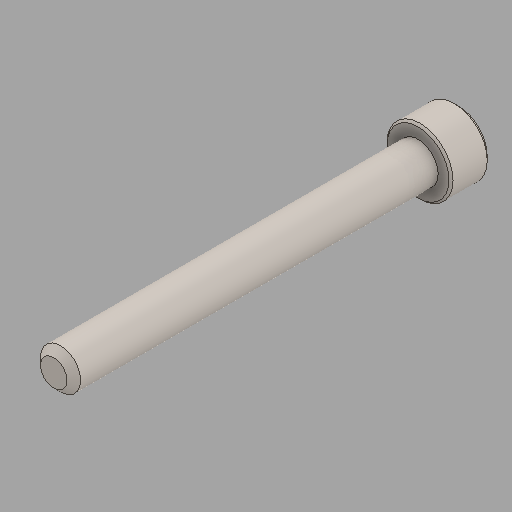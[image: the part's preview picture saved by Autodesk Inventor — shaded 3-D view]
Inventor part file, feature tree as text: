
AUTODESK INVENTOR PART (.ipt)
format: ipt  version: 2024.2 (Build 282272000, 272)  size: 112,640 bytes
history: native  units: in
note: dims shown in document units (in); Inventor stores cm internally (conversion verified against a paired STEP export)
features: chamfer x1
ambient origin geometry x8: Origin, YZ Plane, XZ Plane, XY Plane, X Axis, Y Axis, Z Axis, Center Point
bodies: Solid1 (feature_tree)
feature tree (1):
  chamfer  "Chamfer2"  [1 undecoded]
note: 1 required parameter value undecoded (feature->parameter linkage not recoverable at this tier; creation-order binding heuristic only, values carry confidence <= 0.55)
